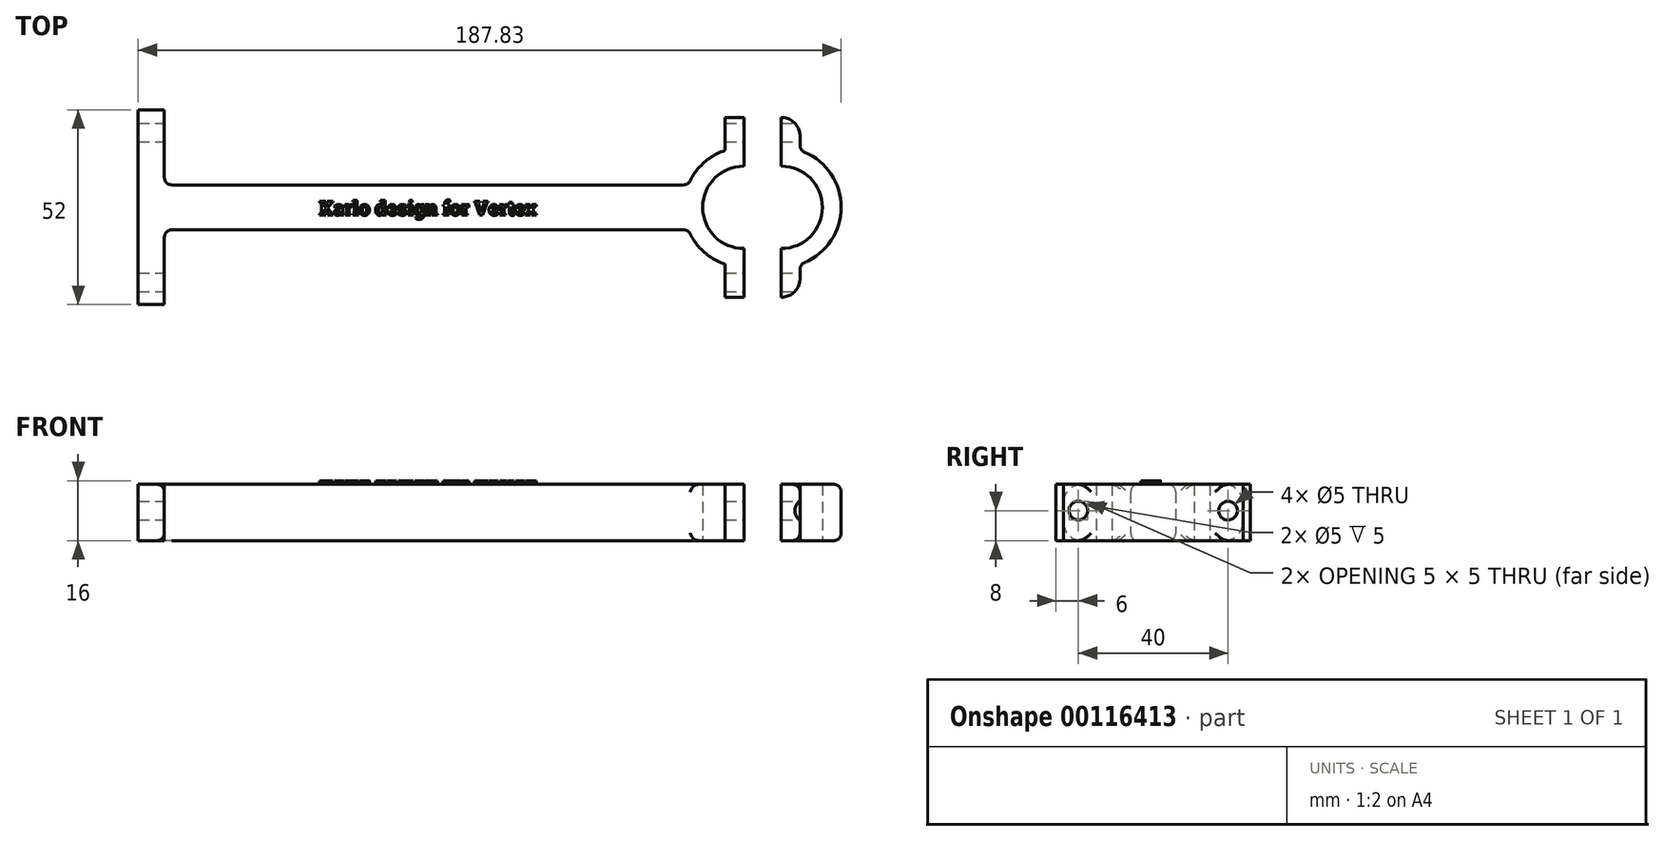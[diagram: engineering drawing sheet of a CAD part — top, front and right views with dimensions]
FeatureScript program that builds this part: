
annotation { "Feature Type Name" : "Feature", "Feature Type Description" : "" }
export const myFeature = defineFeature(function(context is Context, id is Id, definition is map)
    precondition{}
    {
        {
            var Q0;
            Q0=qCreatedBy(makeId("Top.planeOp"),FACE);
            var sketch = newSketch(context, id + "F0", { "sketchPlane" : qUnion([Q0])});
            skArc(sketch, "E0", {"start": v(0, 16) * mm, "mid": v(-16, 0) * mm, "end": v(0, -16) * mm});
            skLineSegment(sketch, "E1", {"start": v(-14.83, 6) * mm, "end": v(-154.83, 6) * mm});
            skLineSegment(sketch, "E2", {"start": v(-14.83, -6) * mm, "end": v(-154.83, -6) * mm});
            skLineSegment(sketch, "E3", {"start": v(-154.83, -6) * mm, "end": v(-154.83, -26) * mm});
            skLineSegment(sketch, "E4", {"start": v(-154.83, -26) * mm, "end": v(-161.83, -26) * mm});
            skLineSegment(sketch, "E5", {"start": v(-161.83, -26) * mm, "end": v(-161.83, 26) * mm});
            skLineSegment(sketch, "E6", {"start": v(-161.83, 26) * mm, "end": v(-154.83, 26) * mm});
            skLineSegment(sketch, "E7", {"start": v(-154.83, 26) * mm, "end": v(-154.83, 6) * mm});
            skArc(sketch, "E8", {"start": v(0, 11) * mm, "mid": v(-11, 0) * mm, "end": v(0, -11) * mm});
            skLineSegment(sketch, "E9", {"start": v(0, 11) * mm, "end": v(0, 16) * mm});
            skLineSegment(sketch, "E10", {"start": v(0, -16) * mm, "end": v(0, -11) * mm});
            skLineSegment(sketch, "E11", {"start": v(0, 16) * mm, "end": v(0, 24) * mm});
            skLineSegment(sketch, "E12", {"start": v(0, 24) * mm, "end": v(-5, 24) * mm});
            skLineSegment(sketch, "E13", {"start": v(-5, 24) * mm, "end": v(-5, 15.2) * mm});
            skLineSegment(sketch, "E14", {"start": v(0, -16) * mm, "end": v(0, -24) * mm});
            skLineSegment(sketch, "E15", {"start": v(0, -24) * mm, "end": v(-5, -24) * mm});
            skLineSegment(sketch, "E16", {"start": v(-5, -24) * mm, "end": v(-5, -15.2) * mm});
            skLineSegment(sketch, "E17", {"start": v(5, 39.4) * mm, "end": v(5, -37.33) * mm, "construction": true});
            skArc(sketch, "E18.MirrorCS", {"start": v(10, 11) * mm, "mid": v(21, 0) * mm, "end": v(10, -11) * mm});
            skArc(sketch, "E19.MirrorCS", {"start": v(10, 16) * mm, "mid": v(26, 0) * mm, "end": v(10, -16) * mm});
            skLineSegment(sketch, "E20.MirrorCS", {"start": v(10, 11) * mm, "end": v(10, 16) * mm});
            skLineSegment(sketch, "E21.MirrorCS", {"start": v(10, 16) * mm, "end": v(10, 24) * mm});
            skLineSegment(sketch, "E22.MirrorCS", {"start": v(10, 24) * mm, "end": v(15, 24) * mm});
            skLineSegment(sketch, "E23.MirrorCS", {"start": v(15, 24) * mm, "end": v(15, 15.2) * mm});
            skLineSegment(sketch, "E24.MirrorCS", {"start": v(10, -16) * mm, "end": v(10, -24) * mm});
            skLineSegment(sketch, "E25.MirrorCS", {"start": v(10, -24) * mm, "end": v(15, -24) * mm});
            skLineSegment(sketch, "E26.MirrorCS", {"start": v(15, -24) * mm, "end": v(15, -15.2) * mm});
            skLineSegment(sketch, "E27.MirrorCS", {"start": v(10, -16) * mm, "end": v(10, -11) * mm});
            skSolve(sketch);
        }
        {
            var Q0;
            Q0 = qSketchRegion(id + "F0", true);
            extrude(context, id + "F1", {"entities" : qUnion([Q0]), "depth" : 15 * mm});
        }
        {
            var Q0;
            Q0=makeQuery(id+"F1.opExtrude","SWEPT_FACE",FACE,{"disambiguationData":[OSD([sQuery(id+"F0.wireOp",EDGE,"E26.MirrorCS")])]});
            var sketch = newSketch(context, id + "F2", { "sketchPlane" : qUnion([Q0])});
            skLineSegment(sketch, "E28", {"start": v(0, 23.6) * mm, "end": v(0, -14.28) * mm, "construction": true});
            skCircle(sketch, "E29", {"center": v(-20, 8) * mm, "radius": 1.5 * mm, "construction": true});
            skCircle(sketch, "E30.MirrorC", {"center": v(20, 8) * mm, "radius": 1.5 * mm, "construction": true});
            skSolve(sketch);
        }
        {
            var Q0;
            Q0=sQuery(id+"F2.wireOp",VERTEX,"E29.center");
            var Q1;
            Q1=sQuery(id+"F2.wireOp",VERTEX,"E30.MirrorC.center");
            var Q2;
            Q2=makeQuery(id+"F1.opExtrude","SWEPT_BODY",BODY,{"disambiguationData":[OSD([sQuery(id+"F0.wireOp",EDGE,"E18.MirrorCS"),sQuery(id+"F0.wireOp",EDGE,"E19.MirrorCS"),sQuery(id+"F0.wireOp",EDGE,"E20.MirrorCS"),sQuery(id+"F0.wireOp",EDGE,"E21.MirrorCS"),sQuery(id+"F0.wireOp",EDGE,"E22.MirrorCS"),sQuery(id+"F0.wireOp",EDGE,"E23.MirrorCS"),sQuery(id+"F0.wireOp",EDGE,"E24.MirrorCS"),sQuery(id+"F0.wireOp",EDGE,"E25.MirrorCS"),sQuery(id+"F0.wireOp",EDGE,"E26.MirrorCS"),sQuery(id+"F0.wireOp",EDGE,"E27.MirrorCS")])]});
            var Q3;
            Q3=makeQuery(id+"F1.opExtrude","SWEPT_BODY",BODY,{"disambiguationData":[OSD([sQuery(id+"F0.wireOp",EDGE,"E0"),sQuery(id+"F0.wireOp",EDGE,"E1"),sQuery(id+"F0.wireOp",EDGE,"E2"),sQuery(id+"F0.wireOp",EDGE,"E3"),sQuery(id+"F0.wireOp",EDGE,"E4"),sQuery(id+"F0.wireOp",EDGE,"E5"),sQuery(id+"F0.wireOp",EDGE,"E6"),sQuery(id+"F0.wireOp",EDGE,"E7"),sQuery(id+"F0.wireOp",EDGE,"E8"),sQuery(id+"F0.wireOp",EDGE,"E9"),sQuery(id+"F0.wireOp",EDGE,"E10"),sQuery(id+"F0.wireOp",EDGE,"E11"),sQuery(id+"F0.wireOp",EDGE,"E12"),sQuery(id+"F0.wireOp",EDGE,"E13"),sQuery(id+"F0.wireOp",EDGE,"E14"),sQuery(id+"F0.wireOp",EDGE,"E15"),sQuery(id+"F0.wireOp",EDGE,"E16")])]});
            hole(context, id + "F3", {"style" : HoleStyle.SIMPLE, "endStyle" : HoleEndStyle.THROUGH, "holeDiameter" : 5 * mm, "locations" : qUnion([Q0, Q1]), "scope" : qUnion([Q2, Q3]), "isTappedThrough" : true});
        }
        {
            var Q0;
            Q0=makeQuery(id+"F1.opExtrude","SWEPT_FACE",FACE,{"disambiguationData":[OSD([sQuery(id+"F0.wireOp",EDGE,"E19.MirrorCS")])]});
            fillet(context, id + "F4", {"entities" : qUnion([Q0]), "radius" : 2 * mm, "tangentPropagation" : true, "allowEdgeOverflow" : false});
        }
        {
            var Q0;
            Q0=makeQuery(id+"F1.opExtrude","SWEPT_EDGE",EDGE,{"disambiguationData":[OSD([sQuery(id+"F0.wireOp",EDGE,"E22.MirrorCS"),sQuery(id+"F0.wireOp",EDGE,"E23.MirrorCS")])]});
            var Q1;
            Q1=makeQuery(id+"F1.opExtrude","SWEPT_EDGE",EDGE,{"disambiguationData":[OSD([sQuery(id+"F0.wireOp",EDGE,"E25.MirrorCS"),sQuery(id+"F0.wireOp",EDGE,"E26.MirrorCS")])]});
            fillet(context, id + "F5", {"entities" : qUnion([Q0, Q1]), "radius" : 5 * mm, "tangentPropagation" : true, "allowEdgeOverflow" : false});
        }
        {
            var Q0;
            Q0=makeQuery(id+"F1.opExtrude","SWEPT_FACE",FACE,{"disambiguationData":[OSD([sQuery(id+"F0.wireOp",EDGE,"E2")])]});
            var Q1;
            Q1=makeQuery(id+"F1.opExtrude","SWEPT_FACE",FACE,{"disambiguationData":[OSD([sQuery(id+"F0.wireOp",EDGE,"E1")])]});
            fillet(context, id + "F6", {"entities" : qUnion([Q0, Q1]), "radius" : 2 * mm, "tangentPropagation" : true, "allowEdgeOverflow" : false});
        }
        {
            var Q0;
            Q0=makeQuery(id+"F1.opExtrude","CAP_EDGE",EDGE,{"disambiguationData":[OSD([sQuery(id+"F0.wireOp",EDGE,"E12")])],"isStart":false});
            var Q1;
            Q1=makeQuery(id+"F1.opExtrude","CAP_EDGE",EDGE,{"disambiguationData":[OSD([sQuery(id+"F0.wireOp",EDGE,"E12")])],"isStart":true});
            var Q2;
            Q2=makeQuery(id+"F1.opExtrude","CAP_EDGE",EDGE,{"disambiguationData":[OSD([sQuery(id+"F0.wireOp",EDGE,"E15")])],"isStart":false});
            var Q3;
            Q3=makeQuery(id+"F1.opExtrude","CAP_EDGE",EDGE,{"disambiguationData":[OSD([sQuery(id+"F0.wireOp",EDGE,"E15")])],"isStart":true});
            fillet(context, id + "F7", {"entities" : qUnion([Q0, Q1, Q2, Q3]), "radius" : 5 * mm, "tangentPropagation" : true, "allowEdgeOverflow" : false});
        }
        {
            var Q0;
            Q0=makeQuery(id+"F1.opExtrude","CAP_FACE",FACE,{"disambiguationData":[OSD([sQuery(id+"F0.wireOp",EDGE,"E0"),sQuery(id+"F0.wireOp",EDGE,"E1"),sQuery(id+"F0.wireOp",EDGE,"E2"),sQuery(id+"F0.wireOp",EDGE,"E3"),sQuery(id+"F0.wireOp",EDGE,"E4"),sQuery(id+"F0.wireOp",EDGE,"E5"),sQuery(id+"F0.wireOp",EDGE,"E6"),sQuery(id+"F0.wireOp",EDGE,"E7"),sQuery(id+"F0.wireOp",EDGE,"E8"),sQuery(id+"F0.wireOp",EDGE,"E9"),sQuery(id+"F0.wireOp",EDGE,"E10"),sQuery(id+"F0.wireOp",EDGE,"E11"),sQuery(id+"F0.wireOp",EDGE,"E12"),sQuery(id+"F0.wireOp",EDGE,"E13"),sQuery(id+"F0.wireOp",EDGE,"E14"),sQuery(id+"F0.wireOp",EDGE,"E15"),sQuery(id+"F0.wireOp",EDGE,"E16")])],"isStart":false});
            var sketch = newSketch(context, id + "F8", { "sketchPlane" : qUnion([Q0])});
            skText(sketch, "E31", { "text": "Karlo design for Vertex", "fontName": "RobotoSlab-Bold.ttf"});
            const initialGuessF8  = {"E31": [-0.11345, -0.0021, 1, 0, 0.00381]};
            skSetInitialGuess(sketch, initialGuessF8);
            skSolve(sketch);
        }
        {
            var Q0;
            Q0 = qSketchRegion(id + "F8", true);
            extrude(context, id + "F9", {"entities" : qUnion([Q0]), "operationType" : NewBodyOperationType.ADD, "depth" : 1 * mm});
        }
    });
